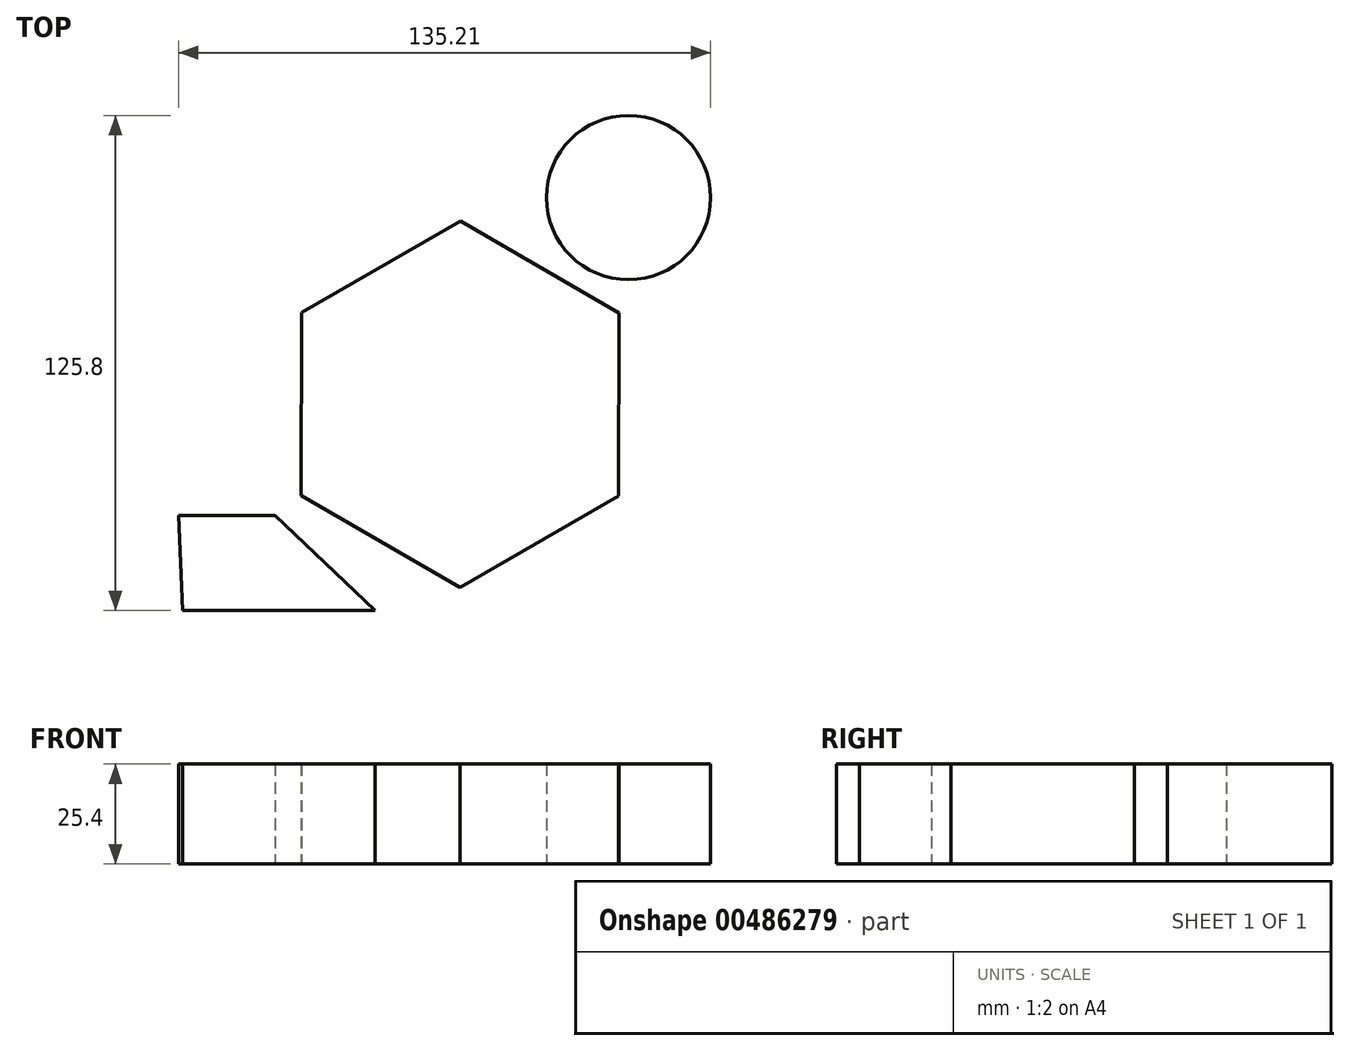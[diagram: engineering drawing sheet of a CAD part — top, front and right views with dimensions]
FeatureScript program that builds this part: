
annotation { "Feature Type Name" : "Feature", "Feature Type Description" : "" }
export const myFeature = defineFeature(function(context is Context, id is Id, definition is map)
    precondition{}
    {
        {
            var Q0;
            Q0=qCreatedBy(makeId("Top.planeOp"),FACE);
            var sketch = newSketch(context, id + "F0", { "sketchPlane" : qUnion([Q0])});
            skCircle(sketch, "E0.cCircle", {"center": v(0, 0) * mm, "radius": 40.32 * mm, "construction": true});
            skLineSegment(sketch, "E0.0", {"start": v(-40.28, 23.35) * mm, "end": v(0.08, 46.56) * mm});
            skLineSegment(sketch, "E0.1", {"start": v(0.08, 46.56) * mm, "end": v(40.36, 23.21) * mm});
            skLineSegment(sketch, "E0.2", {"start": v(40.36, 23.21) * mm, "end": v(40.28, -23.35) * mm});
            skLineSegment(sketch, "E0.3", {"start": v(40.28, -23.35) * mm, "end": v(-0.08, -46.56) * mm});
            skLineSegment(sketch, "E0.4", {"start": v(-0.08, -46.56) * mm, "end": v(-40.36, -23.21) * mm});
            skLineSegment(sketch, "E0.5", {"start": v(-40.36, -23.21) * mm, "end": v(-40.28, 23.35) * mm});
            skPoint(sketch, "E0.0.midPoint", {"position": v(-20.1, 34.96) * mm});
            skSolve(sketch);
        }
        {
            var Q0;
            Q0 = qSketchRegion(id + "F0", true);
            extrude(context, id + "F1", {"entities" : qUnion([Q0]), "depth" : 25.4 * mm});
        }
        {
            var Q0;
            Q0=qCreatedBy(makeId("Top.planeOp"),FACE);
            var sketch = newSketch(context, id + "F2", { "sketchPlane" : qUnion([Q0])});
            skCircle(sketch, "E1", {"center": v(42.77, 52.51) * mm, "radius": 20.87 * mm});
            skSolve(sketch);
        }
        {
            var Q0;
            Q0 = qSketchRegion(id + "F2", true);
            extrude(context, id + "F3", {"entities" : qUnion([Q0]), "depth" : 25.4 * mm});
        }
        {
            var Q0;
            Q0=qCreatedBy(makeId("Top.planeOp"),FACE);
            var sketch = newSketch(context, id + "F4", { "sketchPlane" : qUnion([Q0])});
            skLineSegment(sketch, "E2", {"start": v(-71.57, -28.28) * mm, "end": v(-47, -28.28) * mm});
            skLineSegment(sketch, "E3", {"start": v(-47, -28.28) * mm, "end": v(-21.66, -52.42) * mm});
            skLineSegment(sketch, "E4", {"start": v(-21.66, -52.42) * mm, "end": v(-70.56, -52.42) * mm});
            skLineSegment(sketch, "E5", {"start": v(-70.56, -52.42) * mm, "end": v(-71.57, -28.28) * mm});
            skSolve(sketch);
        }
        {
            var Q0;
            Q0 = qSketchRegion(id + "F4", true);
            extrude(context, id + "F5", {"entities" : qUnion([Q0]), "depth" : 25.4 * mm});
        }
    });
